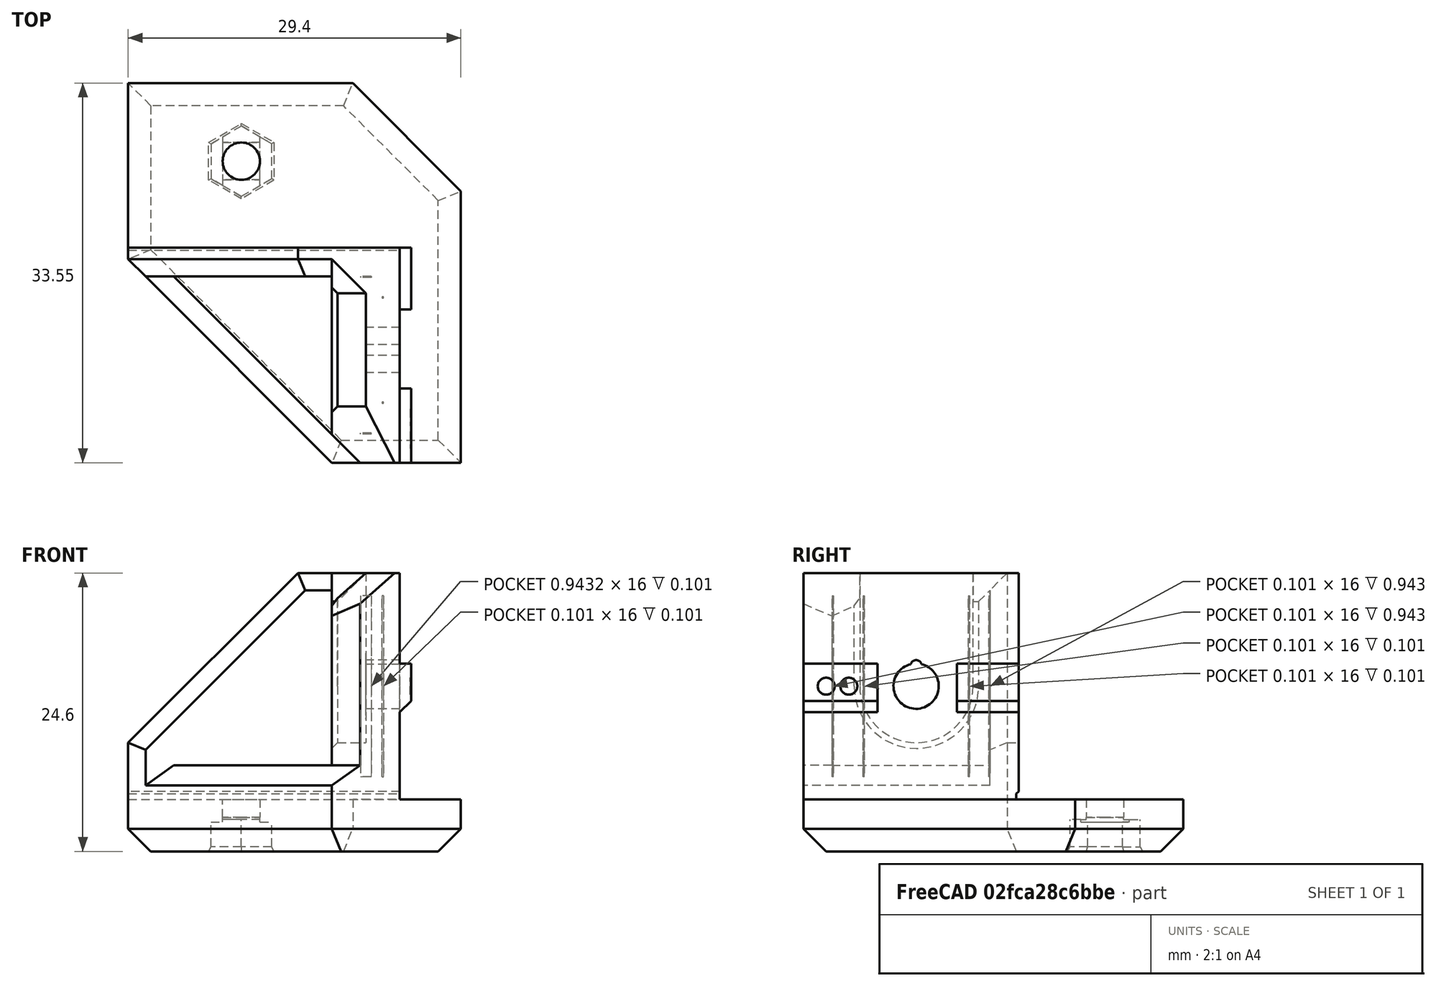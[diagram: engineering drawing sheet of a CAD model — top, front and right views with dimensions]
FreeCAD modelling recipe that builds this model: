
FCSTD DOCUMENT  (FreeCAD 0.18R14555 (Git shallow))
Label: base-top
License: All rights reserved
LicenseURL: http://en.wikipedia.org/wiki/All_rights_reserved
objects: Part::Feature×4, Part::Cut×2, App::Part×1, Part::Box×1, Part::MultiFuse×1
note: 8 computed .brp shape members not serialized (recipe doc carries the construction recipe); baked Part::Feature solids carry a one-line shape summary decoded from their .brp

FEATURE [Part::Feature] Part__Feature001  label="rambo_base_upper_mount"
  Placement = pos=(0,1e-15,4.6) rot=(1,0,0;3.14159rad)
  shape: bbox 29.4 x 33.55 x 24.6 mm, 99 faces (baked)
FEATURE [App::Part] rambo_base_upper_mount_v1  label="rambo_base_upper_mount v1"
  Group = -> [Part__Feature001]
  Origin = -> Origin001
FEATURE [Part::Feature] Part__Feature  label="tslot-vertical-align"
  Placement = pos=(24,-5.3e-15,9.38) rot=(0,0,1;4.71239rad)
  shape: bbox 5 x 60 x 10.45 mm, 10 faces (baked)
FEATURE [Part::Cut] Cut
  Base = -> Part__Feature001
  Tool = -> Part__Feature
FEATURE [Part::Box] Box  label="Cube"
  AttacherType = Attacher::AttachEngine3D
  Height = 10
  Length = 10
  Placement = pos=(24,-27,10) rot=(0,0,1;0rad)
  Width = 7
FEATURE [Part::Cut] Cut001
  Base = -> Cut
  Tool = -> Box
FEATURE [Part::Feature] Part__Feature002  label="m5-to-m4-bolt-hole"
  Placement = pos=(21,-23.6,14.6) rot=(0,0,1;1.5708rad)
  shape: bbox 3 x 6 x 6 mm, 5 faces (baked)
FEATURE [Part::MultiFuse] Fusion
  Shapes = -> [Part__Feature002,Cut001]
FEATURE [Part::Feature] Fusion001
  shape: bbox 29.4 x 33.55 x 24.6 mm, 99 faces (baked)
